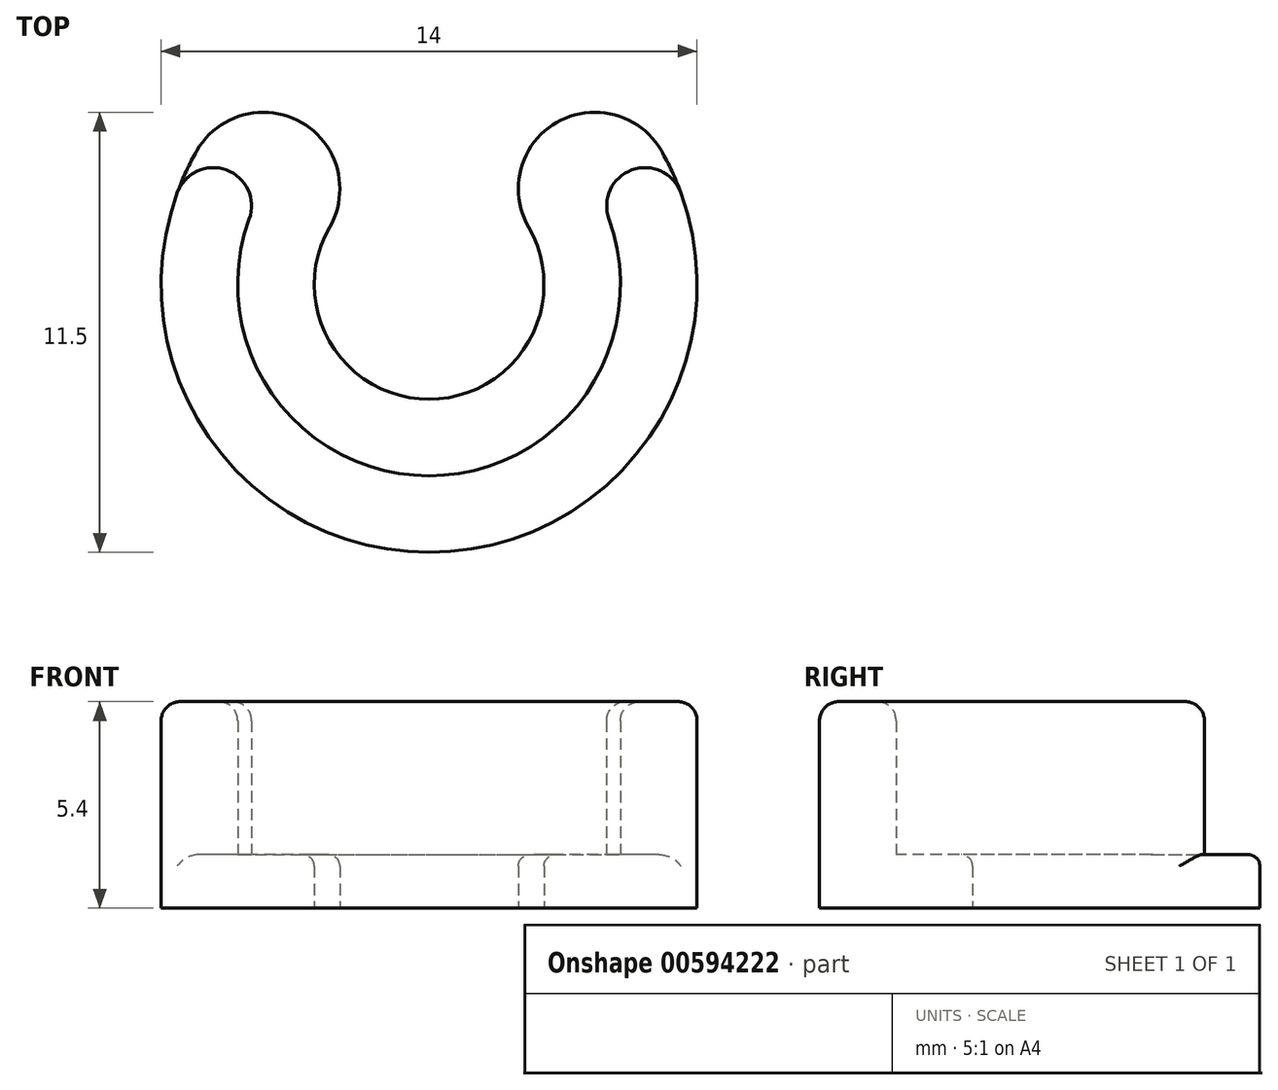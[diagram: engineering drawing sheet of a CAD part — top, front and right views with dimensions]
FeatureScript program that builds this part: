
annotation { "Feature Type Name" : "Feature", "Feature Type Description" : "" }
export const myFeature = defineFeature(function(context is Context, id is Id, definition is map)
    precondition{}
    {
        {
            var Q0;
            Q0=qCreatedBy(makeId("Top.planeOp"),FACE);
            var sketch = newSketch(context, id + "F0", { "sketchPlane" : qUnion([Q0])});
            skArc(sketch, "E0", {"start": v(-2.6, 1.5) * mm, "mid": v(0, -3) * mm, "end": v(2.6, 1.5) * mm});
            skArc(sketch, "E1", {"start": v(-6.06, 3.5) * mm, "mid": v(0, -7) * mm, "end": v(6.06, 3.5) * mm});
            skArc(sketch, "E2", {"start": v(-2.6, 1.5) * mm, "mid": v(-3.33, 4.23) * mm, "end": v(-6.06, 3.5) * mm});
            skArc(sketch, "E3", {"start": v(6.06, 3.5) * mm, "mid": v(3.33, 4.23) * mm, "end": v(2.6, 1.5) * mm});
            skSolve(sketch);
        }
        {
            var Q0;
            Q0 = qSketchRegion(id + "F0", true);
            extrude(context, id + "F1", {"entities" : qUnion([Q0]), "depth" : 1.4 * mm, "offsetDistance" : 25 * mm});
        }
        {
            var Q0;
            Q0=makeQuery(id+"F1.opExtrude","CAP_FACE",FACE,{"disambiguationData":[OSD([sQuery(id+"F0.wireOp",EDGE,"E0"),sQuery(id+"F0.wireOp",EDGE,"E1"),sQuery(id+"F0.wireOp",EDGE,"E2"),sQuery(id+"F0.wireOp",EDGE,"E3")])],"isStart":false});
            var sketch = newSketch(context, id + "F2", { "sketchPlane" : qUnion([Q0])});
            skArc(sketch, "E4", {"start": v(-6.58, 2.4) * mm, "mid": v(0, -7) * mm, "end": v(6.58, 2.4) * mm});
            skArc(sketch, "E5", {"start": v(-4.7, 1.71) * mm, "mid": v(0, -5) * mm, "end": v(4.7, 1.71) * mm});
            skArc(sketch, "E6", {"start": v(-4.7, 1.71) * mm, "mid": v(-5.3, 3) * mm, "end": v(-6.58, 2.4) * mm});
            skArc(sketch, "E7", {"start": v(6.58, 2.4) * mm, "mid": v(5.3, 3) * mm, "end": v(4.7, 1.71) * mm});
            skSolve(sketch);
        }
        {
            var Q0;
            Q0 = qSketchRegion(id + "F2", true);
            extrude(context, id + "F3", {"entities" : qUnion([Q0]), "operationType" : NewBodyOperationType.ADD, "depth" : 4 * mm, "offsetDistance" : 25 * mm});
        }
        {
            var Q0;
            Q0=makeQuery(id+"F3.opExtrude","CAP_EDGE",EDGE,{"disambiguationData":[OSD([sQuery(id+"F2.wireOp",EDGE,"E6")])],"isStart":false});
            fillet(context, id + "F4", {"entities" : qUnion([Q0]), "radius" : .5 * mm, "tangentPropagation" : true, "allowEdgeOverflow" : false});
        }
        {
            var Q0;
            Q0=makeQuery(id+"F1.opExtrude","CAP_EDGE",EDGE,{"disambiguationData":[OSD([sQuery(id+"F0.wireOp",EDGE,"E0")])],"isStart":false});
            var Q1;
            Q1=makeQuery(id+"F1.opExtrude","CAP_EDGE",EDGE,{"disambiguationData":[OSD([sQuery(id+"F0.wireOp",EDGE,"E2")])],"isStart":false});
            var Q2;
            Q2=makeQuery(id+"F1.opExtrude","CAP_EDGE",EDGE,{"disambiguationData":[OSD([sQuery(id+"F0.wireOp",EDGE,"E3")])],"isStart":false});
            fillet(context, id + "F5", {"entities" : qUnion([Q0, Q1, Q2]), "radius" : .3 * mm, "tangentPropagation" : true, "allowEdgeOverflow" : false});
        }
    });
